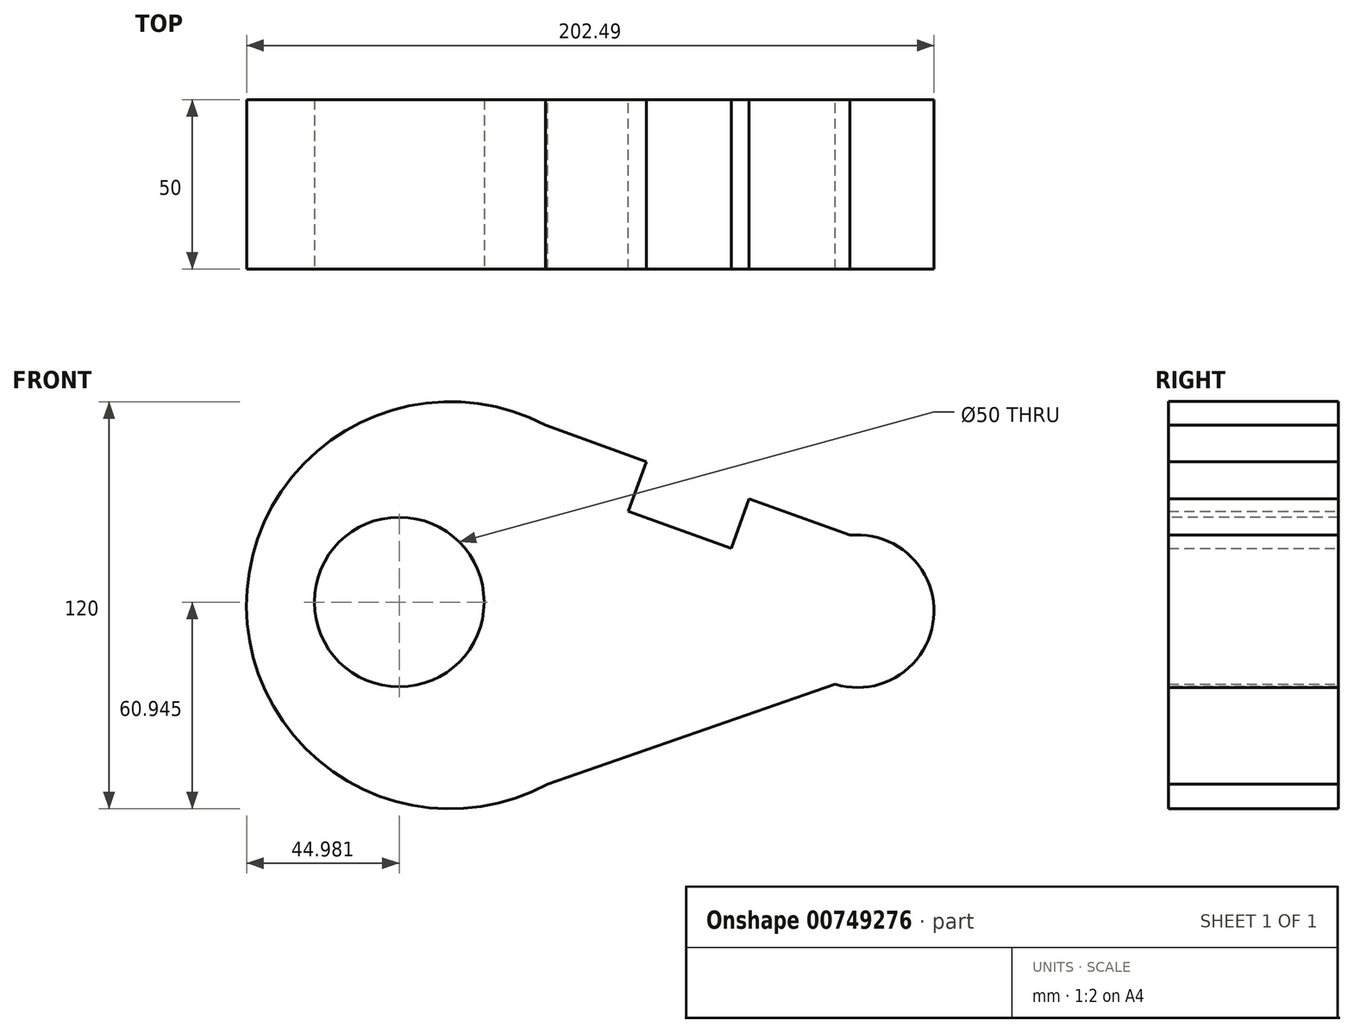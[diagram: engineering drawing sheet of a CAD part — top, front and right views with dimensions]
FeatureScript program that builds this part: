
annotation { "Feature Type Name" : "Feature", "Feature Type Description" : "" }
export const myFeature = defineFeature(function(context is Context, id is Id, definition is map)
    precondition{}
    {
        {
            var Q0;
            Q0=qCreatedBy(makeId("Front.planeOp"),FACE);
            var sketch = newSketch(context, id + "F0", { "sketchPlane" : qUnion([Q0])});
            skCircle(sketch, "E0", {"center": v(-68.27, 23.28) * mm, "radius": 60 * mm});
            skCircle(sketch, "E1", {"center": v(51.72, 21.53) * mm, "radius": 22.5 * mm});
            skLineSegment(sketch, "E2", {"start": v(-40.23, 76.33) * mm, "end": v(49.45, 43.91) * mm});
            skLineSegment(sketch, "E3", {"start": v(45.18, 0) * mm, "end": v(-39.51, -29.38) * mm});
            skSolve(sketch);
        }
        {
            var Q0;
            Q0 = qSketchRegion(id + "F0", true);
            extrude(context, id + "F1", {"entities" : qUnion([Q0]), "depth" : 50 * mm, "offsetDistance" : 25 * mm});
        }
        {
            var Q0;
            Q0=makeQuery(id+"F1.opExtrude","SWEPT_FACE",FACE,{"disambiguationData":[OSD([sQuery(id+"F0.wireOp",EDGE,"E2")])]});
            var sketch = newSketch(context, id + "F2", { "sketchPlane" : qUnion([Q0])});
            skLineSegment(sketch, "E4.bottom", {"start": v(0, -50) * mm, "end": v(-32.2, -50) * mm});
            skLineSegment(sketch, "E4.top", {"start": v(0, 0) * mm, "end": v(-32.2, 0) * mm});
            skLineSegment(sketch, "E4.left", {"start": v(0, -50) * mm, "end": v(0, 0) * mm});
            skLineSegment(sketch, "E4.right", {"start": v(-32.2, -50) * mm, "end": v(-32.2, 0) * mm});
            skPoint(sketch, "E4.middle", {"position": v(-16.1, -25) * mm});
            skPoint(sketch, "E4.middle.positionSnap0", {"position": v(-16.1, 0) * mm});
            skPoint(sketch, "E4.middle.positionSnap1", {"position": v(-63.78, -25) * mm});
            skPoint(sketch, "E4.centerSnap0", {"position": v(-16.1, 0) * mm});
            skPoint(sketch, "E4.centerSnap1", {"position": v(-63.78, -25) * mm});
            skSolve(sketch);
        }
        {
            var Q0;
            Q0=makeQuery(id+"F2.imprint","IMPRINT",FACE,{"disambiguationData":[TD([[makeQuery(id+"F2.imprint","IMPRINT",EDGE,{"derivedFrom":sQuery(id+"F2.wireOp",EDGE,"E4.bottom")}),1.0]])]});
            extrude(context, id + "F3", {"entities" : qUnion([Q0]), "operationType" : NewBodyOperationType.REMOVE, "oppositeDirection" : true, "depth" : 15.5 * mm, "offsetDistance" : 25 * mm});
        }
        {
            var Q0;
            Q0=makeQuery(id+"F1.opExtrude","CAP_FACE",FACE,{"disambiguationData":[OSD([sQuery(id+"F0.wireOp",EDGE,"E0"),sQuery(id+"F0.wireOp",EDGE,"E1"),sQuery(id+"F0.wireOp",EDGE,"E2"),sQuery(id+"F0.wireOp",EDGE,"E3")])],"isStart":false});
            var sketch = newSketch(context, id + "F4", { "sketchPlane" : qUnion([Q0])});
            skCircle(sketch, "E5", {"center": v(-83.29, 24.22) * mm, "radius": 25 * mm});
            skSolve(sketch);
        }
        {
            var Q0;
            Q0 = qSketchRegion(id + "F4", true);
            extrude(context, id + "F5", {"entities" : qUnion([Q0]), "operationType" : NewBodyOperationType.REMOVE, "endBound" : BoundingType.THROUGH_ALL, "oppositeDirection" : true, "depth" : 25 * mm, "offsetDistance" : 25 * mm});
        }
    });
